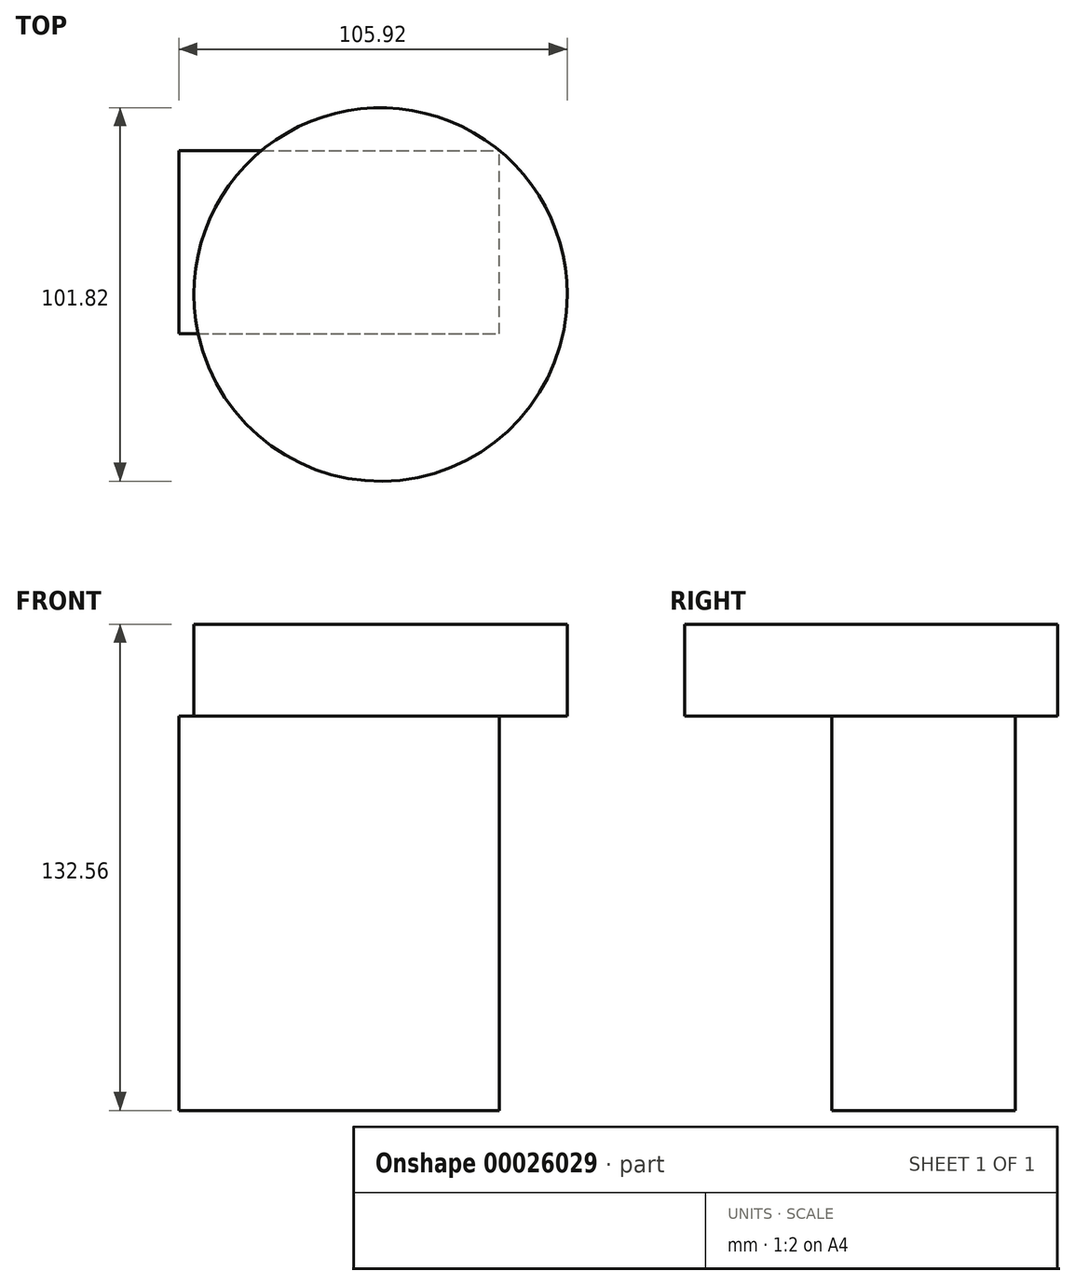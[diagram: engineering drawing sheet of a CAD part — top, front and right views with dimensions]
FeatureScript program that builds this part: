
annotation { "Feature Type Name" : "Feature", "Feature Type Description" : "" }
export const myFeature = defineFeature(function(context is Context, id is Id, definition is map)
    precondition{}
    {
        {
            var Q0;
            Q0=qCreatedBy(makeId("Front.planeOp"),FACE);
            var sketch = newSketch(context, id + "F0", { "sketchPlane" : qUnion([Q0])});
            skLineSegment(sketch, "E0.bottom", {"start": v(-43.16, 0) * mm, "end": v(44.25, 0) * mm});
            skLineSegment(sketch, "E0.top", {"start": v(-43.16, 107.56) * mm, "end": v(44.25, 107.56) * mm});
            skLineSegment(sketch, "E0.left", {"start": v(-43.16, 0) * mm, "end": v(-43.16, 107.56) * mm});
            skLineSegment(sketch, "E0.right", {"start": v(44.25, 0) * mm, "end": v(44.25, 107.56) * mm});
            skSolve(sketch);
        }
        {
            var Q0;
            Q0=makeQuery(id+"F0.imprint","IMPRINT",FACE,{"disambiguationData":[TD([[makeQuery(id+"F0.imprint","IMPRINT",EDGE,{"derivedFrom":sQuery(id+"F0.wireOp",EDGE,"E0.bottom")}),1.0]])]});
            extrude(context, id + "F1", {"entities" : qUnion([Q0]), "depth" : 25 * mm, "hasSecondDirection" : true, "secondDirectionOppositeDirection" : true, "secondDirectionDepth" : 25 * mm});
        }
        {
            var Q0;
            Q0=makeQuery(id+"F1.opExtrude","SWEPT_FACE",FACE,{"disambiguationData":[OSD([sQuery(id+"F0.wireOp",EDGE,"E0.top")])]});
            var sketch = newSketch(context, id + "F2", { "sketchPlane" : qUnion([Q0])});
            skCircle(sketch, "E1", {"center": v(11.85, -14.27) * mm, "radius": 50.91 * mm});
            skSolve(sketch);
        }
        {
            var Q0;
            Q0 = qSketchRegion(id + "F2", true);
            extrude(context, id + "F3", {"entities" : qUnion([Q0]), "operationType" : NewBodyOperationType.ADD, "depth" : 25 * mm});
        }
    });
